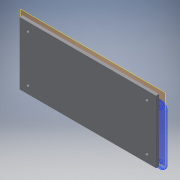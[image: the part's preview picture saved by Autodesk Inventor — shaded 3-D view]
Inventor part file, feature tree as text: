
AUTODESK INVENTOR PART (.ipt)
format: ipt  version: 2019 (Build 230136000, 136)  size: 221,184 bytes
history: native  units: mm
features: reference x6, extrude x4, sketch x4, other x3, plane x2, fillet x1
ambient origin geometry x8: Origin, YZ Plane, XZ Plane, XY Plane, X Axis, Y Axis, Z Axis, Center Point
bodies: Volumenkörper1 (feature_tree)
feature tree (20):
  plane  "Arbeitsebene1"
  extrude  "Extrusion1"  Depth=6.0mm
  plane  "Arbeitsebene2"
  extrude  "Extrusion2"  Depth=6.0mm
  extrude  "Extrusion3"  Depth=3.0mm
  fillet  "Rundung1"  Radius=7.0mm
  extrude  "Extrusion5"  Depth=7.0mm
  sketch  "Skizze1"  dims[d0=6.0mm d1=6.0mm]
  reference  "Referenz1"
  reference  "Referenz2"
  reference  "Referenz3"
  reference  "Referenz4"
  sketch  "Skizze2"  dims[d2=6.0mm d3=6.0mm]
  reference  "Referenz5"
  reference  "Referenz6"
  sketch  "Skizze3"  dims[d4=3.0mm d5=0.0mm d6=3.0mm d7=7.0mm]
  sketch  "Skizze5"  dims[d8=7.0mm d9=7.0mm d10=7.0mm d11=3.0mm d12=15.0mm d13=15.0mm d14=15.0mm d15=15.0mm d16=5.0mm d17=29.0mm d18=14.0mm d19=20.0mm d20=18.0mm d21=7.0mm d22=7.0mm d23=12.0mm d24=5.0mm d25=13.0mm d26=30.0mm d27=31.0mm d28=3.0mm d29=0.0mm d31=8.0mm d32=8.0mm d33=8.0mm d34=8.0mm d35=3.0mm d36=0.0mm d37=3.75mm d44=12.0mm d45=12.0mm d46=12.0mm d47=12.0mm d48=2.0mm d49=0.0mm]
  other  "<userpath>\Google Drive\Projekte\makroboard\makroboard_case\Baugruppe1.iam"
  other  "Baugruppe1.iam"
  other  "makroboard:1"
